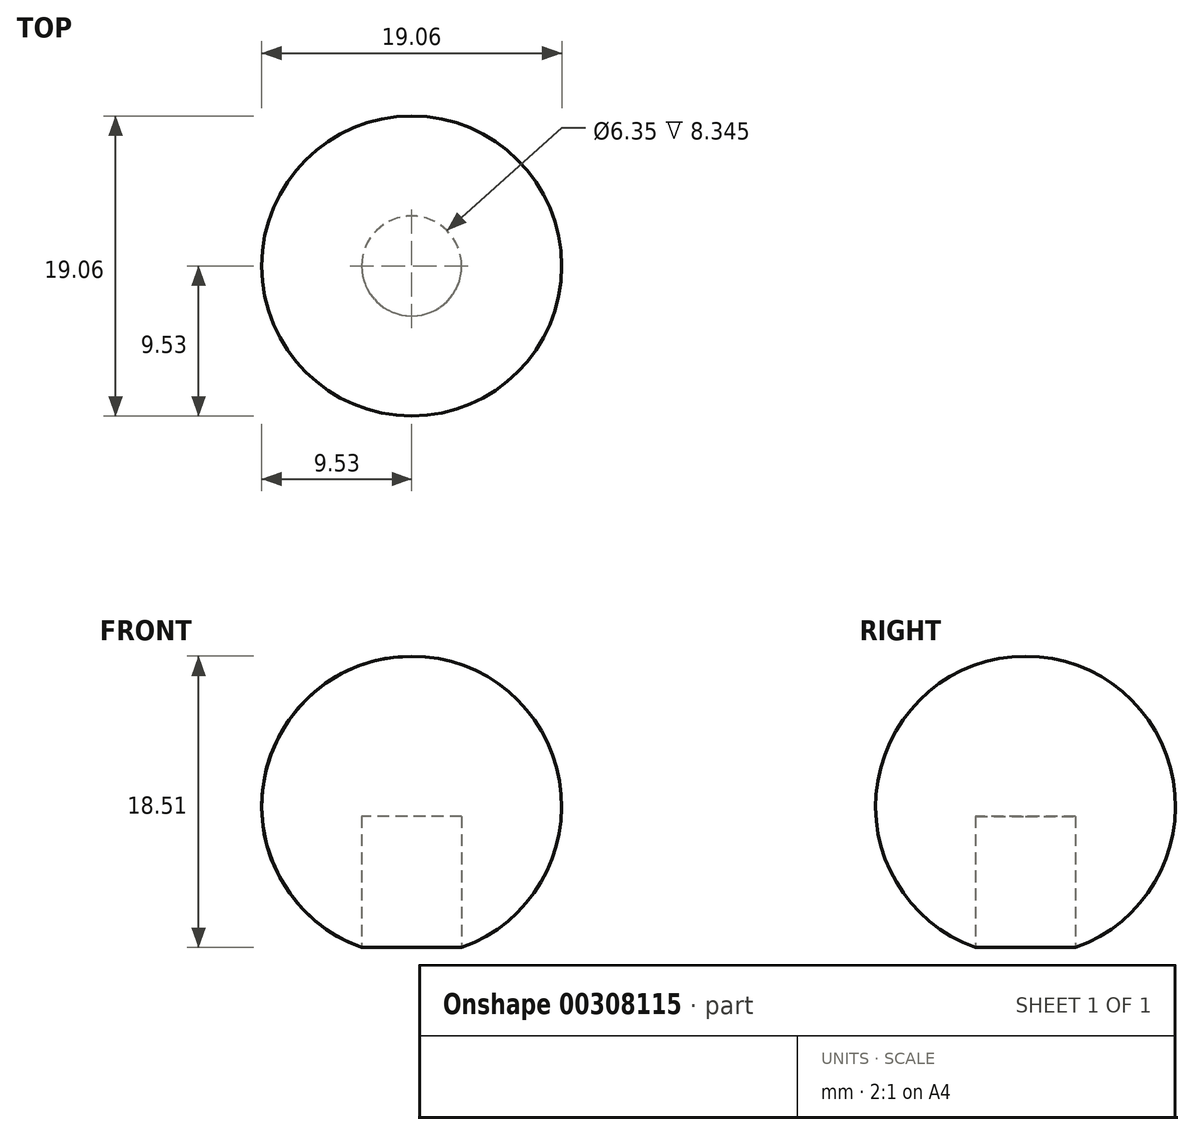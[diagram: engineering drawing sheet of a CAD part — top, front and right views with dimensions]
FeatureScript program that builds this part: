
annotation { "Feature Type Name" : "Feature", "Feature Type Description" : "" }
export const myFeature = defineFeature(function(context is Context, id is Id, definition is map)
    precondition{}
    {
        {
            var Q0;
            Q0=qCreatedBy(makeId("Front.planeOp"),FACE);
            var sketch = newSketch(context, id + "F0", { "sketchPlane" : qUnion([Q0])});
            skArc(sketch, "E0", {"start": v(0, 9.53) * mm, "mid": v(-9.53, 0) * mm, "end": v(0, -9.53) * mm});
            skLineSegment(sketch, "E1", {"start": v(0, 9.53) * mm, "end": v(0, -9.53) * mm});
            skSolve(sketch);
        }
        {
            var Q0;
            Q0=qCreatedBy(makeId("Top.planeOp"),FACE);
            var sketch = newSketch(context, id + "F1", { "sketchPlane" : qUnion([Q0])});
            skCircle(sketch, "E2", {"center": v(0, 0) * mm, "radius": 9.53 * mm});
            skSolve(sketch);
        }
        {
            var Q0;
            Q0=makeQuery(id+"F0.imprint","IMPRINT",FACE,{"disambiguationData":[TD([[makeQuery(id+"F0.imprint","IMPRINT",EDGE,{"derivedFrom":sQuery(id+"F0.wireOp",EDGE,"E0")}),1.0]])]});
            var Q1;
            Q1=sQuery(id+"F1.wireOp",EDGE,"E2");
            revolve(context, id + "F2", {"entities" : qUnion([Q0]), "axis" : qUnion([Q1]), "revolveType" : RevolveType.FULL});
        }
        {
            var Q0;
            Q0=qCreatedBy(makeId("Top.planeOp"),FACE);
            cPlane(context, id + "F3", {"entities" : qUnion([Q0]), "cplaneType" : CPlaneType.OFFSET, "offset" : 10.16 * mm, "oppositeDirection" : true, "width" : 152.4 * mm, "height" : 152.4 * mm});
        }
        {
            var Q0;
            Q0=qCreatedBy(id+"F3.planeOp",FACE);
            var sketch = newSketch(context, id + "F4", { "sketchPlane" : qUnion([Q0])});
            skCircle(sketch, "E3", {"center": v(0, 0) * mm, "radius": 3.18 * mm});
            skSolve(sketch);
        }
        {
            var Q0;
            Q0 = qSketchRegion(id + "F4", true);
            extrude(context, id + "F5", {"entities" : qUnion([Q0]), "operationType" : NewBodyOperationType.REMOVE, "depth" : 9.52 * mm});
        }
    });
